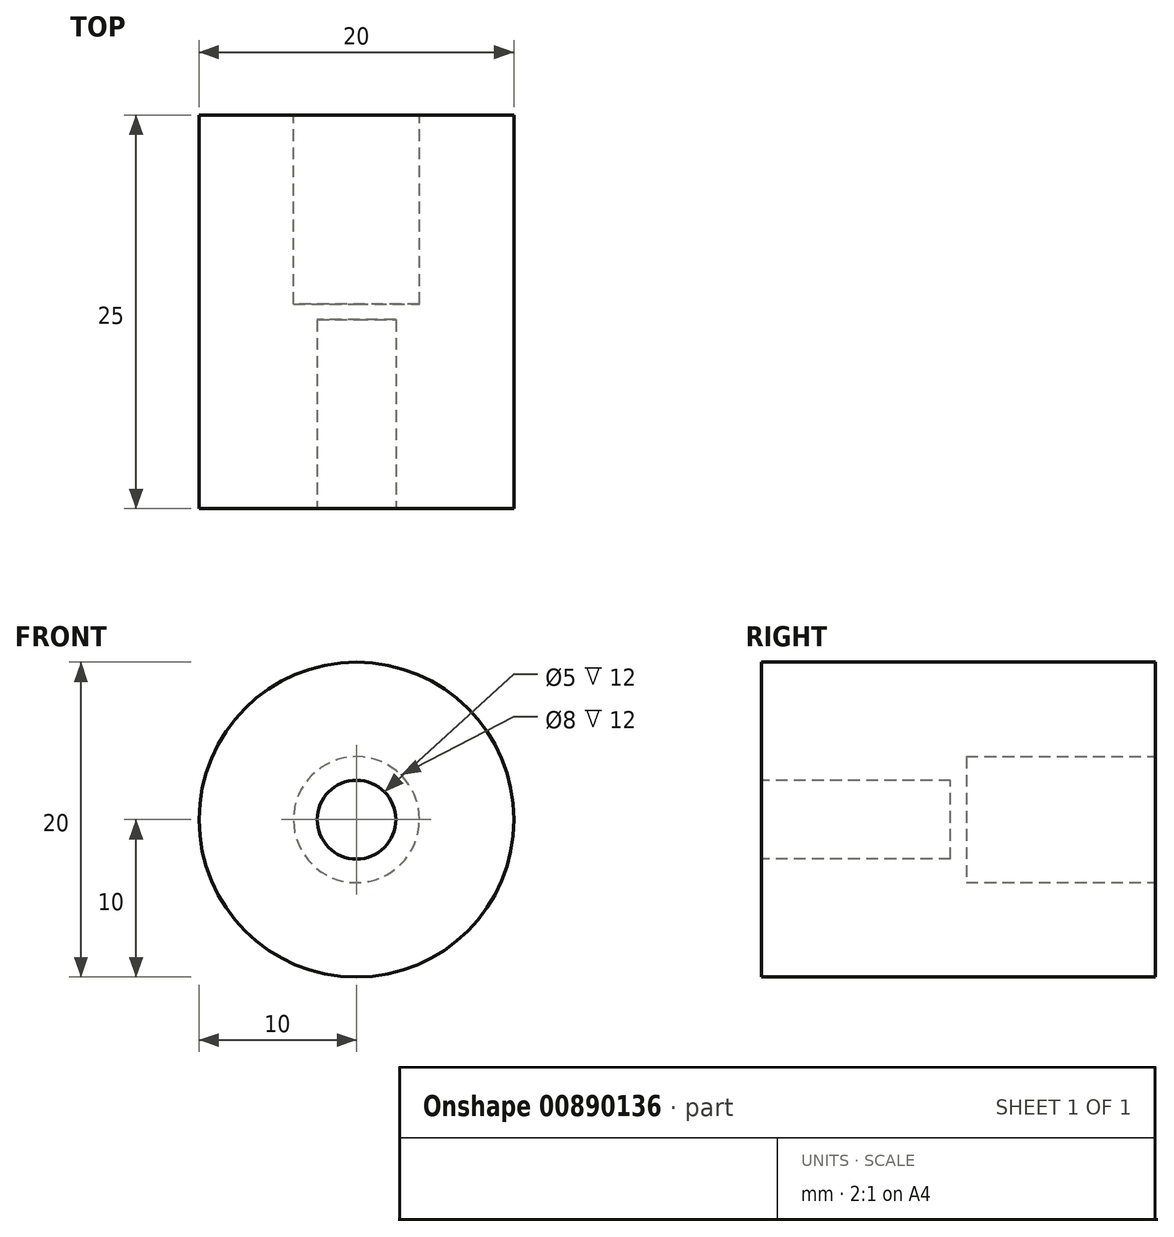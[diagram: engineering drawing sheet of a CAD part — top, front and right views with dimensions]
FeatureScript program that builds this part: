
annotation { "Feature Type Name" : "Feature", "Feature Type Description" : "" }
export const myFeature = defineFeature(function(context is Context, id is Id, definition is map)
    precondition{}
    {
        {
            var Q0;
            Q0=qCreatedBy(makeId("Front.planeOp"),FACE);
            var sketch = newSketch(context, id + "F0", { "sketchPlane" : qUnion([Q0])});
            skCircle(sketch, "E0", {"center": v(0, 0) * mm, "radius": 10 * mm});
            skSolve(sketch);
        }
        {
            var Q0;
            Q0=makeQuery(id+"F0.imprint","IMPRINT",FACE,{"disambiguationData":[TD([[makeQuery(id+"F0.imprint","IMPRINT",EDGE,{"derivedFrom":sQuery(id+"F0.wireOp",EDGE,"E0")}),1.0]])]});
            extrude(context, id + "F1", {"entities" : qUnion([Q0]), "depth" : 25 * mm, "offsetDistance" : 25 * mm, "symmetric" : true});
        }
        {
            var Q0;
            Q0=makeQuery(id+"F1.opExtrude","CAP_FACE",FACE,{"disambiguationData":[OSD([sQuery(id+"F0.wireOp",EDGE,"E0")])],"isStart":false});
            var sketch = newSketch(context, id + "F2", { "sketchPlane" : qUnion([Q0])});
            skCircle(sketch, "E1", {"center": v(0, 0) * mm, "radius": 2.5 * mm});
            skSolve(sketch);
        }
        {
            var Q0;
            Q0=qSketchRegion(id+"F2",true);
            extrude(context, id + "F3", {"entities" : qUnion([Q0]), "operationType" : NewBodyOperationType.REMOVE, "oppositeDirection" : true, "depth" : 12 * mm, "offsetDistance" : 25 * mm});
        }
        {
            var Q0;
            Q0=makeQuery(id+"F1.opExtrude","CAP_FACE",FACE,{"disambiguationData":[OSD([sQuery(id+"F0.wireOp",EDGE,"E0")])],"isStart":true});
            var sketch = newSketch(context, id + "F4", { "sketchPlane" : qUnion([Q0])});
            skCircle(sketch, "E2", {"center": v(0, 0) * mm, "radius": 4 * mm});
            skSolve(sketch);
        }
        {
            var Q0;
            Q0=qSketchRegion(id+"F4",true);
            extrude(context, id + "F5", {"entities" : qUnion([Q0]), "operationType" : NewBodyOperationType.REMOVE, "oppositeDirection" : true, "depth" : 12 * mm, "offsetDistance" : 25 * mm});
        }
    });
